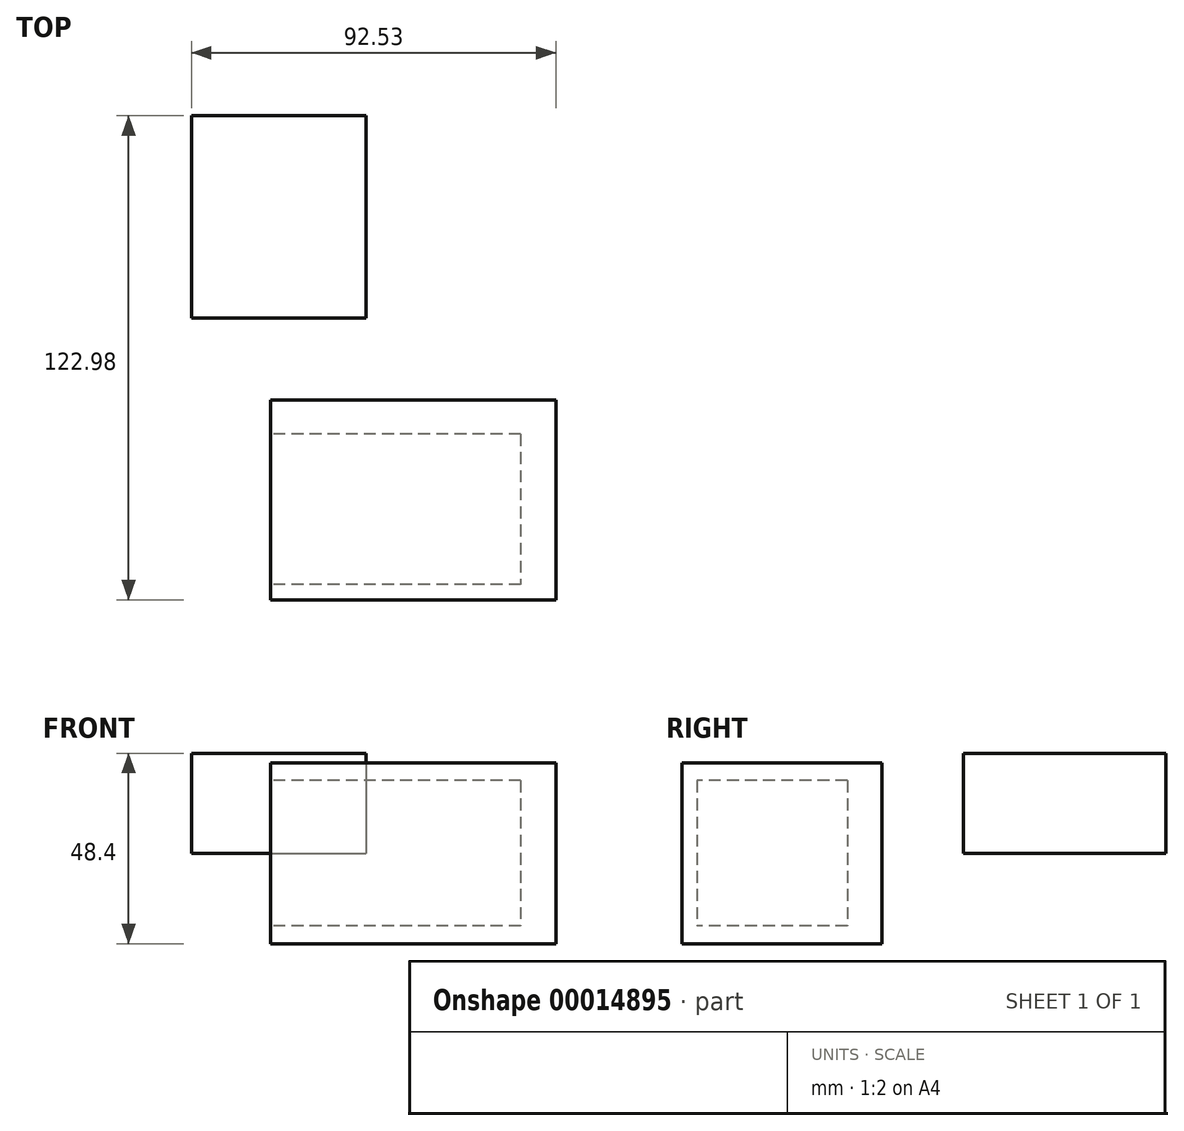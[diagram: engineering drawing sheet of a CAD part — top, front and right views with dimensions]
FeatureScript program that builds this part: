
annotation { "Feature Type Name" : "Feature", "Feature Type Description" : "" }
export const myFeature = defineFeature(function(context is Context, id is Id, definition is map)
    precondition{}
    {
        {
            var Q0;
            Q0=qCreatedBy(makeId("Front.planeOp"),FACE);
            var sketch = newSketch(context, id + "F0", { "sketchPlane" : qUnion([Q0])});
            skLineSegment(sketch, "E0.rect.bottom", {"start": v(-36.22, 23) * mm, "end": v(36.22, 23) * mm});
            skLineSegment(sketch, "E0.rect.top", {"start": v(-36.22, -23) * mm, "end": v(36.22, -23) * mm});
            skLineSegment(sketch, "E0.rect.left", {"start": v(-36.22, 23) * mm, "end": v(-36.22, -23) * mm});
            skLineSegment(sketch, "E0.rect.right", {"start": v(36.22, 23) * mm, "end": v(36.22, -23) * mm});
            skPoint(sketch, "E0.rect.middle", {"position": v(0, 0) * mm});
            skSolve(sketch);
        }
        {
            var Q0;
            Q0=makeQuery(id+"F0.imprint","IMPRINT",FACE,{"disambiguationData":[TD([[makeQuery(id+"F0.imprint","IMPRINT",EDGE,{"derivedFrom":sQuery(id+"F0.wireOp",EDGE,"E0.rect.bottom")}),-1.0]])]});
            extrude(context, id + "F1", {"entities" : qUnion([Q0]), "depth" : 50.8 * mm});
        }
        {
            var Q0;
            Q0=makeQuery(id+"F1.opExtrude","SWEPT_FACE",FACE,{"disambiguationData":[OSD([sQuery(id+"F0.wireOp",EDGE,"E0.rect.left")])]});
            var sketch = newSketch(context, id + "F2", { "sketchPlane" : qUnion([Q0])});
            skLineSegment(sketch, "E1.rect.bottom", {"start": v(8.71, 18.49) * mm, "end": v(46.93, 18.49) * mm});
            skLineSegment(sketch, "E1.rect.top", {"start": v(8.71, -18.49) * mm, "end": v(46.93, -18.49) * mm});
            skLineSegment(sketch, "E1.rect.left", {"start": v(8.71, 18.49) * mm, "end": v(8.71, -18.49) * mm});
            skLineSegment(sketch, "E1.rect.right", {"start": v(46.93, 18.49) * mm, "end": v(46.93, -18.49) * mm});
            skPoint(sketch, "E1.rect.middle", {"position": v(27.82, 0) * mm});
            skSolve(sketch);
        }
        {
            var Q0;
            Q0=makeQuery(id+"F2.imprint","IMPRINT",FACE,{"disambiguationData":[TD([[makeQuery(id+"F2.imprint","IMPRINT",EDGE,{"derivedFrom":sQuery(id+"F2.wireOp",EDGE,"E1.rect.bottom")}),-1.0]])]});
            extrude(context, id + "F3", {"entities" : qUnion([Q0]), "operationType" : NewBodyOperationType.REMOVE, "oppositeDirection" : true, "depth" : 63.5 * mm});
        }
        {
            var Q0;
            Q0=qCreatedBy(makeId("Top.planeOp"),FACE);
            var sketch = newSketch(context, id + "F4", { "sketchPlane" : qUnion([Q0])});
            skLineSegment(sketch, "E2.rect.bottom", {"start": v(-56.3, 72.18) * mm, "end": v(-11.98, 72.18) * mm});
            skLineSegment(sketch, "E2.rect.top", {"start": v(-56.3, 20.72) * mm, "end": v(-11.98, 20.72) * mm});
            skLineSegment(sketch, "E2.rect.left", {"start": v(-56.3, 72.18) * mm, "end": v(-56.3, 20.72) * mm});
            skLineSegment(sketch, "E2.rect.right", {"start": v(-11.98, 72.18) * mm, "end": v(-11.98, 20.72) * mm});
            skPoint(sketch, "E2.rect.middle", {"position": v(-34.14, 46.45) * mm});
            skSolve(sketch);
        }
        {
            var Q0;
            Q0=makeQuery(id+"F4.imprint","IMPRINT",FACE,{"disambiguationData":[TD([[makeQuery(id+"F4.imprint","IMPRINT",EDGE,{"derivedFrom":sQuery(id+"F4.wireOp",EDGE,"E2.rect.bottom")}),-1.0]])]});
            extrude(context, id + "F5", {"entities" : qUnion([Q0]), "depth" : 25.4 * mm});
        }
    });
